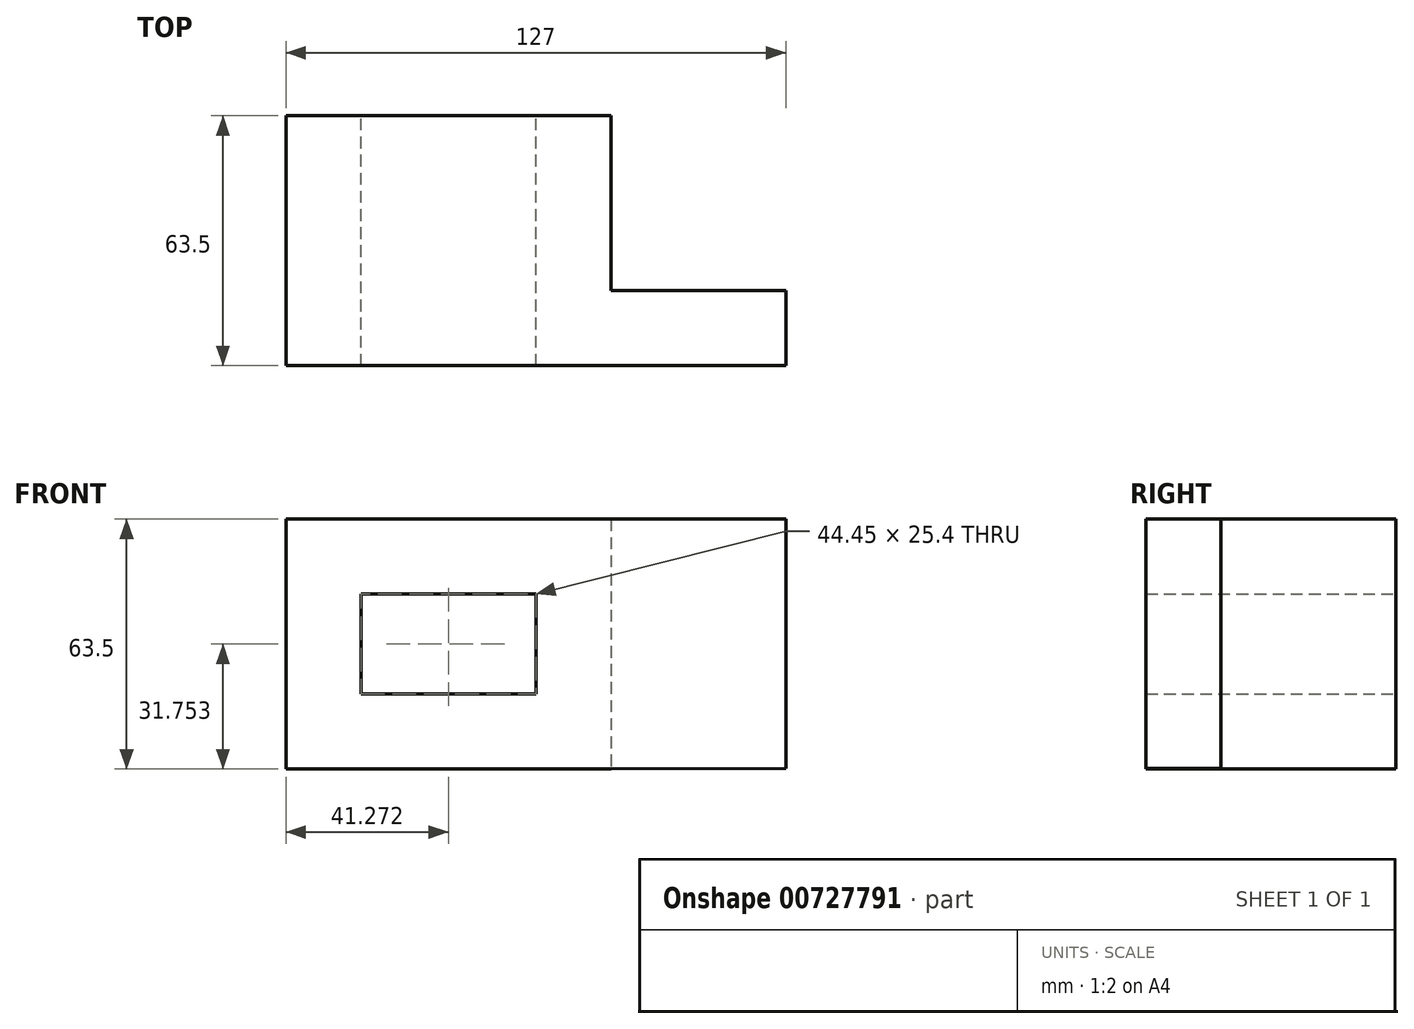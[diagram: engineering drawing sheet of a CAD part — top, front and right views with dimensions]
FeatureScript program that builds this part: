
annotation { "Feature Type Name" : "Feature", "Feature Type Description" : "" }
export const myFeature = defineFeature(function(context is Context, id is Id, definition is map)
    precondition{}
    {
        {
            var Q0;
            Q0=qCreatedBy(makeId("Front.planeOp"),FACE);
            var sketch = newSketch(context, id + "F0", { "sketchPlane" : qUnion([Q0])});
            skLineSegment(sketch, "E0", {"start": v(-45.62, 63.32) * mm, "end": v(36.93, 63.32) * mm});
            skLineSegment(sketch, "E1", {"start": v(36.93, 63.32) * mm, "end": v(36.93, -0.18) * mm});
            skLineSegment(sketch, "E2", {"start": v(36.93, -0.18) * mm, "end": v(-45.62, -0.18) * mm});
            skLineSegment(sketch, "E3", {"start": v(-45.62, -0.18) * mm, "end": v(-45.62, 63.32) * mm});
            skLineSegment(sketch, "E4", {"start": v(-26.57, 44.27) * mm, "end": v(17.88, 44.27) * mm});
            skLineSegment(sketch, "E5", {"start": v(17.88, 44.27) * mm, "end": v(17.88, 18.87) * mm});
            skLineSegment(sketch, "E6", {"start": v(17.88, 18.87) * mm, "end": v(-26.57, 18.87) * mm});
            skLineSegment(sketch, "E7", {"start": v(-26.57, 18.87) * mm, "end": v(-26.57, 44.27) * mm});
            skLineSegment(sketch, "E8", {"start": v(36.93, 63.32) * mm, "end": v(81.38, 63.32) * mm});
            skLineSegment(sketch, "E9", {"start": v(81.38, 63.32) * mm, "end": v(81.38, 0) * mm});
            skLineSegment(sketch, "E10", {"start": v(81.38, 0) * mm, "end": v(36.93, -0.18) * mm});
            skSolve(sketch);
        }
        {
            var Q0;
            Q0 = qSketchRegion(id + "F0", true);
            extrude(context, id + "F1", {"entities" : qUnion([Q0]), "depth" : 19.05 * mm, "offsetDistance" : 25.4 * mm});
        }
        {
            var Q0;
            Q0=makeQuery(id+"F0.imprint","IMPRINT",FACE,{"disambiguationData":[TD([[makeQuery(id+"F0.imprint","IMPRINT",EDGE,{"derivedFrom":sQuery(id+"F0.wireOp",EDGE,"E0")}),-1.0]])]});
            extrude(context, id + "F2", {"entities" : qUnion([Q0]), "operationType" : NewBodyOperationType.ADD, "oppositeDirection" : true, "depth" : 44.45 * mm, "offsetDistance" : 25.4 * mm});
        }
    });
